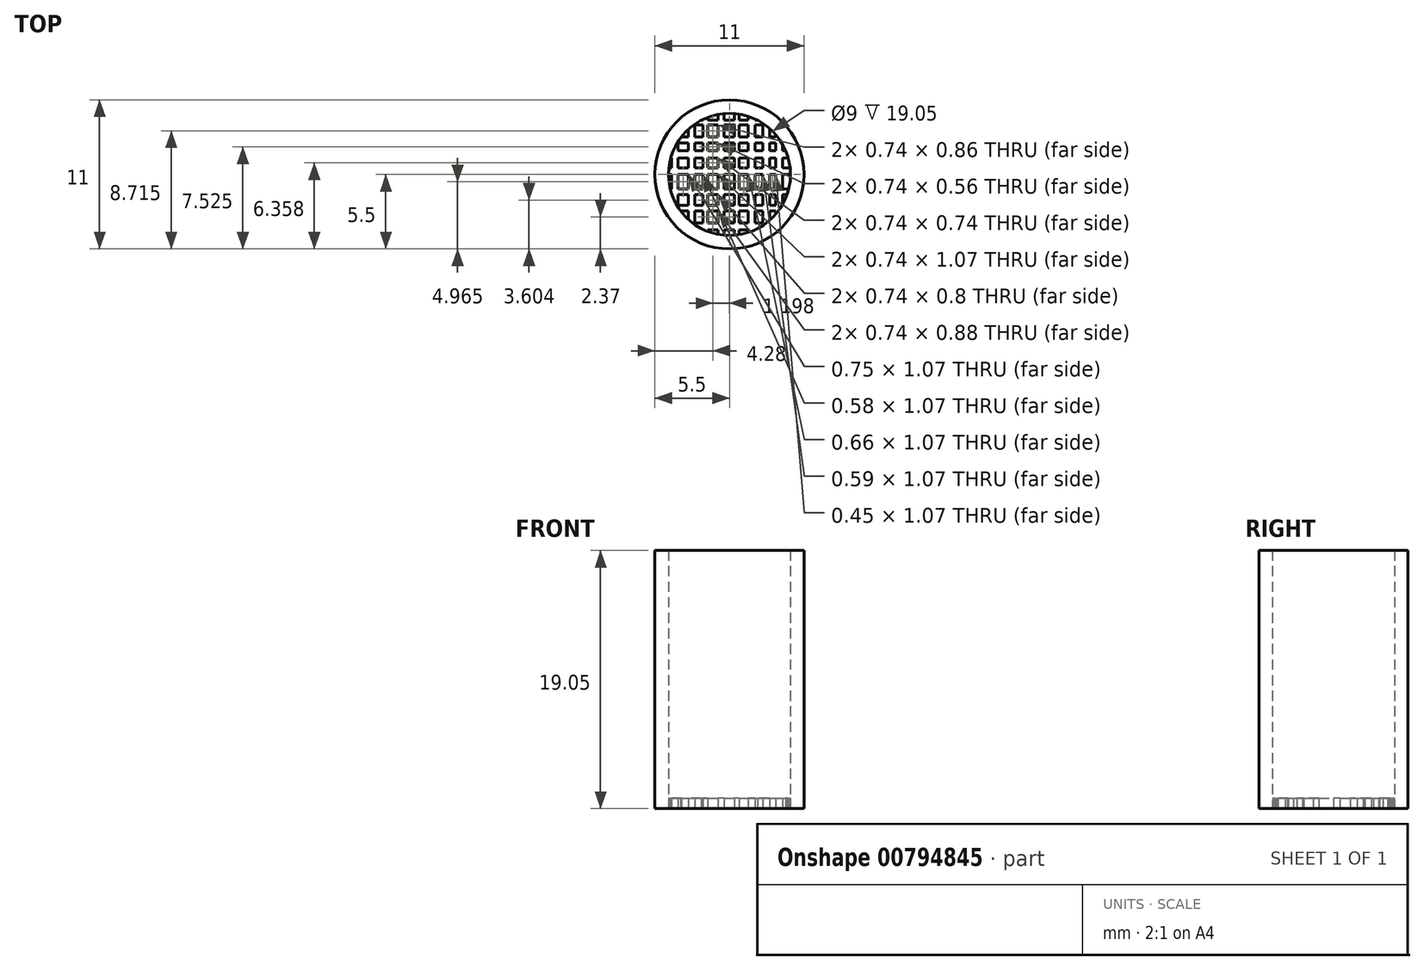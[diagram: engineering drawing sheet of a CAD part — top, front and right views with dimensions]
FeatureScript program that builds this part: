
annotation { "Feature Type Name" : "Feature", "Feature Type Description" : "" }
export const myFeature = defineFeature(function(context is Context, id is Id, definition is map)
    precondition{}
    {
        {
            var Q0;
            Q0=qCreatedBy(makeId("Top.planeOp"),FACE);
            var sketch = newSketch(context, id + "F0", { "sketchPlane" : qUnion([Q0])});
            skCircle(sketch, "E0", {"center": v(0, 0) * mm, "radius": 5.5 * mm});
            skSolve(sketch);
        }
        {
            var Q0;
            Q0=makeQuery(id+"F0.imprint","IMPRINT",FACE,{"disambiguationData":[TD([[makeQuery(id+"F0.imprint","IMPRINT",EDGE,{"derivedFrom":sQuery(id+"F0.wireOp",EDGE,"E0")}),1.0]])]});
            var Q1;
            Q1=sQuery(id+"F0.wireOp",EDGE,"E0");
            extrude(context, id + "F1", {"entities" : qUnion([Q0]), "surfaceEntities" : qUnion([Q1]), "depth" : 19.05 * mm, "offsetDistance" : 25.4 * mm});
        }
        {
            var Q0;
            Q0=qCreatedBy(makeId("Top.planeOp"),FACE);
            var sketch = newSketch(context, id + "F2", { "sketchPlane" : qUnion([Q0])});
            skCircle(sketch, "E1", {"center": v(0, 0) * mm, "radius": 4.5 * mm});
            skSolve(sketch);
        }
        {
            var Q0;
            Q0=makeQuery(id+"F2.imprint","IMPRINT",FACE,{"disambiguationData":[TD([[makeQuery(id+"F2.imprint","IMPRINT",EDGE,{"derivedFrom":sQuery(id+"F2.wireOp",EDGE,"E1")}),1.0]])]});
            extrude(context, id + "F3", {"entities" : qUnion([Q0]), "operationType" : NewBodyOperationType.REMOVE, "depth" : 76.7 * mm, "offsetDistance" : 25.4 * mm});
        }
        {
            var Q0;
            Q0=qCreatedBy(makeId("Top.planeOp"),FACE);
            var sketch = newSketch(context, id + "F4", { "sketchPlane" : qUnion([Q0])});
            skLineSegment(sketch, "E2.bottom", {"start": v(-4.27, -3.14) * mm, "end": v(-3.78, -3.14) * mm});
            skLineSegment(sketch, "E2.top", {"start": v(-4.27, 3.15) * mm, "end": v(-3.78, 3.15) * mm});
            skLineSegment(sketch, "E2.left", {"start": v(-4.27, -3.14) * mm, "end": v(-4.27, 3.15) * mm});
            skLineSegment(sketch, "E2.right", {"start": v(-3.78, -3.14) * mm, "end": v(-3.78, 3.15) * mm});
            skSolve(sketch);
        }
        {
            var Q0;
            Q0=makeQuery(id+"F4.imprint","IMPRINT",FACE,{"disambiguationData":[TD([[makeQuery(id+"F4.imprint","IMPRINT",EDGE,{"derivedFrom":sQuery(id+"F4.wireOp",EDGE,"E2.bottom")}),1.0]])]});
            extrude(context, id + "F5", {"entities" : qUnion([Q0]), "operationType" : NewBodyOperationType.ADD, "depth" : 0.76 * mm, "offsetDistance" : 25.4 * mm});
        }
        {
            var Q0;
            Q0=qCreatedBy(makeId("Top.planeOp"),FACE);
            var sketch = newSketch(context, id + "F6", { "sketchPlane" : qUnion([Q0])});
            skLineSegment(sketch, "E3.bottom", {"start": v(-3.03, -4) * mm, "end": v(-2.55, -4) * mm});
            skLineSegment(sketch, "E3.top", {"start": v(-3.03, 4.04) * mm, "end": v(-2.55, 4.04) * mm});
            skLineSegment(sketch, "E3.left", {"start": v(-3.03, -4) * mm, "end": v(-3.03, 4.04) * mm});
            skLineSegment(sketch, "E3.right", {"start": v(-2.55, -4) * mm, "end": v(-2.55, 4.04) * mm});
            skSolve(sketch);
        }
        {
            var Q0;
            Q0=makeQuery(id+"F6.imprint","IMPRINT",FACE,{"disambiguationData":[TD([[makeQuery(id+"F6.imprint","IMPRINT",EDGE,{"derivedFrom":sQuery(id+"F6.wireOp",EDGE,"E3.bottom")}),1.0]])]});
            extrude(context, id + "F7", {"entities" : qUnion([Q0]), "operationType" : NewBodyOperationType.ADD, "depth" : 0.76 * mm, "offsetDistance" : 25.4 * mm});
        }
        {
            var Q0;
            Q0=qCreatedBy(makeId("Top.planeOp"),FACE);
            var sketch = newSketch(context, id + "F8", { "sketchPlane" : qUnion([Q0])});
            skLineSegment(sketch, "E4.bottom", {"start": v(-1.96, -4.6) * mm, "end": v(-1.6, -4.6) * mm});
            skLineSegment(sketch, "E4.top", {"start": v(-1.96, 4.74) * mm, "end": v(-1.6, 4.74) * mm});
            skLineSegment(sketch, "E4.left", {"start": v(-1.96, -4.6) * mm, "end": v(-1.96, 4.74) * mm});
            skLineSegment(sketch, "E4.right", {"start": v(-1.6, -4.6) * mm, "end": v(-1.6, 4.74) * mm});
            skSolve(sketch);
        }
        {
            var Q0;
            Q0=makeQuery(id+"F8.imprint","IMPRINT",FACE,{"disambiguationData":[TD([[makeQuery(id+"F8.imprint","IMPRINT",EDGE,{"derivedFrom":sQuery(id+"F8.wireOp",EDGE,"E4.bottom")}),1.0]])]});
            extrude(context, id + "F9", {"entities" : qUnion([Q0]), "operationType" : NewBodyOperationType.ADD, "depth" : 0.76 * mm, "offsetDistance" : 25.4 * mm});
        }
        {
            var Q0;
            Q0=qCreatedBy(makeId("Top.planeOp"),FACE);
            var sketch = newSketch(context, id + "F10", { "sketchPlane" : qUnion([Q0])});
            skLineSegment(sketch, "E5.bottom", {"start": v(-0.85, -5.13) * mm, "end": v(-0.4, -5.13) * mm});
            skLineSegment(sketch, "E5.top", {"start": v(-0.85, 5) * mm, "end": v(-0.4, 5) * mm});
            skLineSegment(sketch, "E5.left", {"start": v(-0.85, -5.13) * mm, "end": v(-0.85, 5) * mm});
            skLineSegment(sketch, "E5.right", {"start": v(-0.4, -5.13) * mm, "end": v(-0.4, 5) * mm});
            skSolve(sketch);
        }
        {
            var Q0;
            Q0=makeQuery(id+"F10.imprint","IMPRINT",FACE,{"disambiguationData":[TD([[makeQuery(id+"F10.imprint","IMPRINT",EDGE,{"derivedFrom":sQuery(id+"F10.wireOp",EDGE,"E5.bottom")}),1.0]])]});
            extrude(context, id + "F11", {"entities" : qUnion([Q0]), "operationType" : NewBodyOperationType.ADD, "depth" : 0.76 * mm, "offsetDistance" : 25.4 * mm});
        }
        {
            var Q0;
            Q0=qCreatedBy(makeId("Top.planeOp"),FACE);
            var sketch = newSketch(context, id + "F12", { "sketchPlane" : qUnion([Q0])});
            skLineSegment(sketch, "E6.bottom", {"start": v(0.35, -5) * mm, "end": v(0.72, -5) * mm});
            skLineSegment(sketch, "E6.top", {"start": v(0.35, 4.95) * mm, "end": v(0.72, 4.95) * mm});
            skLineSegment(sketch, "E6.left", {"start": v(0.35, -5) * mm, "end": v(0.35, 4.95) * mm});
            skLineSegment(sketch, "E6.right", {"start": v(0.72, -5) * mm, "end": v(0.72, 4.95) * mm});
            skSolve(sketch);
        }
        {
            var Q0;
            Q0=makeQuery(id+"F12.imprint","IMPRINT",FACE,{"disambiguationData":[TD([[makeQuery(id+"F12.imprint","IMPRINT",EDGE,{"derivedFrom":sQuery(id+"F12.wireOp",EDGE,"E6.bottom")}),1.0]])]});
            extrude(context, id + "F13", {"entities" : qUnion([Q0]), "operationType" : NewBodyOperationType.ADD, "depth" : 0.76 * mm, "offsetDistance" : 25.4 * mm});
        }
        {
            var Q0;
            Q0=qCreatedBy(makeId("Top.planeOp"),FACE);
            var sketch = newSketch(context, id + "F14", { "sketchPlane" : qUnion([Q0])});
            skLineSegment(sketch, "E7.bottom", {"start": v(1.38, -4.88) * mm, "end": v(1.88, -4.88) * mm});
            skLineSegment(sketch, "E7.top", {"start": v(1.38, 4.62) * mm, "end": v(1.88, 4.62) * mm});
            skLineSegment(sketch, "E7.left", {"start": v(1.38, -4.88) * mm, "end": v(1.38, 4.62) * mm});
            skLineSegment(sketch, "E7.right", {"start": v(1.88, -4.88) * mm, "end": v(1.88, 4.62) * mm});
            skSolve(sketch);
        }
        {
            var Q0;
            Q0=makeQuery(id+"F14.imprint","IMPRINT",FACE,{"disambiguationData":[TD([[makeQuery(id+"F14.imprint","IMPRINT",EDGE,{"derivedFrom":sQuery(id+"F14.wireOp",EDGE,"E7.bottom")}),1.0]])]});
            extrude(context, id + "F15", {"entities" : qUnion([Q0]), "operationType" : NewBodyOperationType.ADD, "depth" : 0.76 * mm, "offsetDistance" : 25.4 * mm});
        }
        {
            var Q0;
            Q0=qCreatedBy(makeId("Top.planeOp"),FACE);
            var sketch = newSketch(context, id + "F16", { "sketchPlane" : qUnion([Q0])});
            skLineSegment(sketch, "E8.bottom", {"start": v(2.47, -4.47) * mm, "end": v(2.95, -4.47) * mm});
            skLineSegment(sketch, "E8.top", {"start": v(2.47, 4.18) * mm, "end": v(2.95, 4.18) * mm});
            skLineSegment(sketch, "E8.left", {"start": v(2.47, -4.47) * mm, "end": v(2.47, 4.18) * mm});
            skLineSegment(sketch, "E8.right", {"start": v(2.95, -4.47) * mm, "end": v(2.95, 4.18) * mm});
            skSolve(sketch);
        }
        {
            var Q0;
            Q0=makeQuery(id+"F16.imprint","IMPRINT",FACE,{"disambiguationData":[TD([[makeQuery(id+"F16.imprint","IMPRINT",EDGE,{"derivedFrom":sQuery(id+"F16.wireOp",EDGE,"E8.bottom")}),1.0]])]});
            extrude(context, id + "F17", {"entities" : qUnion([Q0]), "operationType" : NewBodyOperationType.ADD, "depth" : 0.76 * mm, "offsetDistance" : 25.4 * mm});
        }
        {
            var Q0;
            Q0=qCreatedBy(makeId("Top.planeOp"),FACE);
            var sketch = newSketch(context, id + "F18", { "sketchPlane" : qUnion([Q0])});
            skLineSegment(sketch, "E9.bottom", {"start": v(3.4, -3.7) * mm, "end": v(3.92, -3.7) * mm});
            skLineSegment(sketch, "E9.top", {"start": v(3.4, 3.35) * mm, "end": v(3.92, 3.35) * mm});
            skLineSegment(sketch, "E9.left", {"start": v(3.4, -3.7) * mm, "end": v(3.4, 3.35) * mm});
            skLineSegment(sketch, "E9.right", {"start": v(3.92, -3.7) * mm, "end": v(3.92, 3.35) * mm});
            skSolve(sketch);
        }
        {
            var Q0;
            Q0=makeQuery(id+"F18.imprint","IMPRINT",FACE,{"disambiguationData":[TD([[makeQuery(id+"F18.imprint","IMPRINT",EDGE,{"derivedFrom":sQuery(id+"F18.wireOp",EDGE,"E9.bottom")}),1.0]])]});
            extrude(context, id + "F19", {"entities" : qUnion([Q0]), "operationType" : NewBodyOperationType.ADD, "depth" : 0.76 * mm, "offsetDistance" : 25.4 * mm});
        }
        {
            var Q0;
            Q0=qCreatedBy(makeId("Top.planeOp"),FACE);
            var sketch = newSketch(context, id + "F20", { "sketchPlane" : qUnion([Q0])});
            skLineSegment(sketch, "E10.bottom", {"start": v(-3.42, -4.1) * mm, "end": v(3.33, -4.1) * mm});
            skLineSegment(sketch, "E10.top", {"start": v(-3.42, -3.57) * mm, "end": v(3.33, -3.57) * mm});
            skLineSegment(sketch, "E10.left", {"start": v(-3.42, -4.1) * mm, "end": v(-3.42, -3.57) * mm});
            skLineSegment(sketch, "E10.right", {"start": v(3.33, -4.1) * mm, "end": v(3.33, -3.57) * mm});
            skSolve(sketch);
        }
        {
            var Q0;
            Q0=makeQuery(id+"F20.imprint","IMPRINT",FACE,{"disambiguationData":[TD([[makeQuery(id+"F20.imprint","IMPRINT",EDGE,{"derivedFrom":sQuery(id+"F20.wireOp",EDGE,"E10.bottom")}),1.0]])]});
            extrude(context, id + "F21", {"entities" : qUnion([Q0]), "operationType" : NewBodyOperationType.ADD, "depth" : 0.76 * mm, "offsetDistance" : 25.4 * mm});
        }
        {
            var Q0;
            Q0=qCreatedBy(makeId("Top.planeOp"),FACE);
            var sketch = newSketch(context, id + "F22", { "sketchPlane" : qUnion([Q0])});
            skLineSegment(sketch, "E11.bottom", {"start": v(-4.08, -2.7) * mm, "end": v(4.2, -2.7) * mm});
            skLineSegment(sketch, "E11.top", {"start": v(-4.08, -2.3) * mm, "end": v(4.2, -2.3) * mm});
            skLineSegment(sketch, "E11.left", {"start": v(-4.08, -2.7) * mm, "end": v(-4.08, -2.3) * mm});
            skLineSegment(sketch, "E11.right", {"start": v(4.2, -2.7) * mm, "end": v(4.2, -2.3) * mm});
            skSolve(sketch);
        }
        {
            var Q0;
            Q0=makeQuery(id+"F22.imprint","IMPRINT",FACE,{"disambiguationData":[TD([[makeQuery(id+"F22.imprint","IMPRINT",EDGE,{"derivedFrom":sQuery(id+"F22.wireOp",EDGE,"E11.bottom")}),1.0]])]});
            extrude(context, id + "F23", {"entities" : qUnion([Q0]), "operationType" : NewBodyOperationType.ADD, "depth" : 0.76 * mm, "offsetDistance" : 25.4 * mm});
        }
        {
            var Q0;
            Q0=qCreatedBy(makeId("Top.planeOp"),FACE);
            var sketch = newSketch(context, id + "F24", { "sketchPlane" : qUnion([Q0])});
            skLineSegment(sketch, "E12.bottom", {"start": v(-4.87, -1.5) * mm, "end": v(5, -1.5) * mm});
            skLineSegment(sketch, "E12.top", {"start": v(-4.87, -1.07) * mm, "end": v(5, -1.07) * mm});
            skLineSegment(sketch, "E12.left", {"start": v(-4.87, -1.5) * mm, "end": v(-4.87, -1.07) * mm});
            skLineSegment(sketch, "E12.right", {"start": v(5, -1.5) * mm, "end": v(5, -1.07) * mm});
            skSolve(sketch);
        }
        {
            var Q0;
            Q0=makeQuery(id+"F24.imprint","IMPRINT",FACE,{"disambiguationData":[TD([[makeQuery(id+"F24.imprint","IMPRINT",EDGE,{"derivedFrom":sQuery(id+"F24.wireOp",EDGE,"E12.bottom")}),1.0]])]});
            extrude(context, id + "F25", {"entities" : qUnion([Q0]), "operationType" : NewBodyOperationType.ADD, "depth" : 0.76 * mm, "offsetDistance" : 25.4 * mm});
        }
        {
            var Q0;
            Q0=qCreatedBy(makeId("Top.planeOp"),FACE);
            var sketch = newSketch(context, id + "F26", { "sketchPlane" : qUnion([Q0])});
            skLineSegment(sketch, "E13.bottom", {"start": v(-4.98, 0) * mm, "end": v(4.97, 0) * mm});
            skLineSegment(sketch, "E13.top", {"start": v(-4.98, 0.49) * mm, "end": v(4.97, 0.49) * mm});
            skLineSegment(sketch, "E13.left", {"start": v(-4.98, 0) * mm, "end": v(-4.98, 0.49) * mm});
            skLineSegment(sketch, "E13.right", {"start": v(4.97, 0) * mm, "end": v(4.97, 0.49) * mm});
            skSolve(sketch);
        }
        {
            var Q0;
            Q0=makeQuery(id+"F26.imprint","IMPRINT",FACE,{"disambiguationData":[TD([[makeQuery(id+"F26.imprint","IMPRINT",EDGE,{"derivedFrom":sQuery(id+"F26.wireOp",EDGE,"E13.bottom")}),1.0]])]});
            extrude(context, id + "F27", {"entities" : qUnion([Q0]), "operationType" : NewBodyOperationType.ADD, "depth" : 0.76 * mm, "offsetDistance" : 25.4 * mm});
        }
        {
            var Q0;
            Q0=qCreatedBy(makeId("Top.planeOp"),FACE);
            var sketch = newSketch(context, id + "F28", { "sketchPlane" : qUnion([Q0])});
            skLineSegment(sketch, "E14.bottom", {"start": v(-4.72, 1.23) * mm, "end": v(4.8, 1.23) * mm});
            skLineSegment(sketch, "E14.top", {"start": v(-4.72, 1.74) * mm, "end": v(4.8, 1.74) * mm});
            skLineSegment(sketch, "E14.left", {"start": v(-4.72, 1.23) * mm, "end": v(-4.72, 1.74) * mm});
            skLineSegment(sketch, "E14.right", {"start": v(4.8, 1.23) * mm, "end": v(4.8, 1.74) * mm});
            skSolve(sketch);
        }
        {
            var Q0;
            Q0=makeQuery(id+"F28.imprint","IMPRINT",FACE,{"disambiguationData":[TD([[makeQuery(id+"F28.imprint","IMPRINT",EDGE,{"derivedFrom":sQuery(id+"F28.wireOp",EDGE,"E14.bottom")}),1.0]])]});
            extrude(context, id + "F29", {"entities" : qUnion([Q0]), "operationType" : NewBodyOperationType.ADD, "depth" : 0.76 * mm, "offsetDistance" : 25.4 * mm});
        }
        {
            var Q0;
            Q0=qCreatedBy(makeId("Top.planeOp"),FACE);
            var sketch = newSketch(context, id + "F30", { "sketchPlane" : qUnion([Q0])});
            skLineSegment(sketch, "E15.bottom", {"start": v(-4.41, 2.3) * mm, "end": v(4.45, 2.3) * mm});
            skLineSegment(sketch, "E15.top", {"start": v(-4.41, 2.78) * mm, "end": v(4.45, 2.78) * mm});
            skLineSegment(sketch, "E15.left", {"start": v(-4.41, 2.3) * mm, "end": v(-4.41, 2.78) * mm});
            skLineSegment(sketch, "E15.right", {"start": v(4.45, 2.3) * mm, "end": v(4.45, 2.78) * mm});
            skSolve(sketch);
        }
        {
            var Q0;
            Q0=makeQuery(id+"F30.imprint","IMPRINT",FACE,{"disambiguationData":[TD([[makeQuery(id+"F30.imprint","IMPRINT",EDGE,{"derivedFrom":sQuery(id+"F30.wireOp",EDGE,"E15.bottom")}),1.0]])]});
            extrude(context, id + "F31", {"entities" : qUnion([Q0]), "operationType" : NewBodyOperationType.ADD, "depth" : 0.76 * mm, "offsetDistance" : 25.4 * mm});
        }
        {
            var Q0;
            Q0=qCreatedBy(makeId("Top.planeOp"),FACE);
            var sketch = newSketch(context, id + "F32", { "sketchPlane" : qUnion([Q0])});
            skLineSegment(sketch, "E16.bottom", {"start": v(-3.16, 3.65) * mm, "end": v(3.29, 3.65) * mm});
            skLineSegment(sketch, "E16.top", {"start": v(-3.16, 4) * mm, "end": v(3.29, 4) * mm});
            skLineSegment(sketch, "E16.left", {"start": v(-3.16, 3.65) * mm, "end": v(-3.16, 4) * mm});
            skLineSegment(sketch, "E16.right", {"start": v(3.29, 3.65) * mm, "end": v(3.29, 4) * mm});
            skSolve(sketch);
        }
        {
            var Q0;
            Q0=makeQuery(id+"F32.imprint","IMPRINT",FACE,{"disambiguationData":[TD([[makeQuery(id+"F32.imprint","IMPRINT",EDGE,{"derivedFrom":sQuery(id+"F32.wireOp",EDGE,"E16.bottom")}),1.0]])]});
            extrude(context, id + "F33", {"entities" : qUnion([Q0]), "operationType" : NewBodyOperationType.ADD, "depth" : 0.76 * mm, "offsetDistance" : 25.4 * mm});
        }
    });
